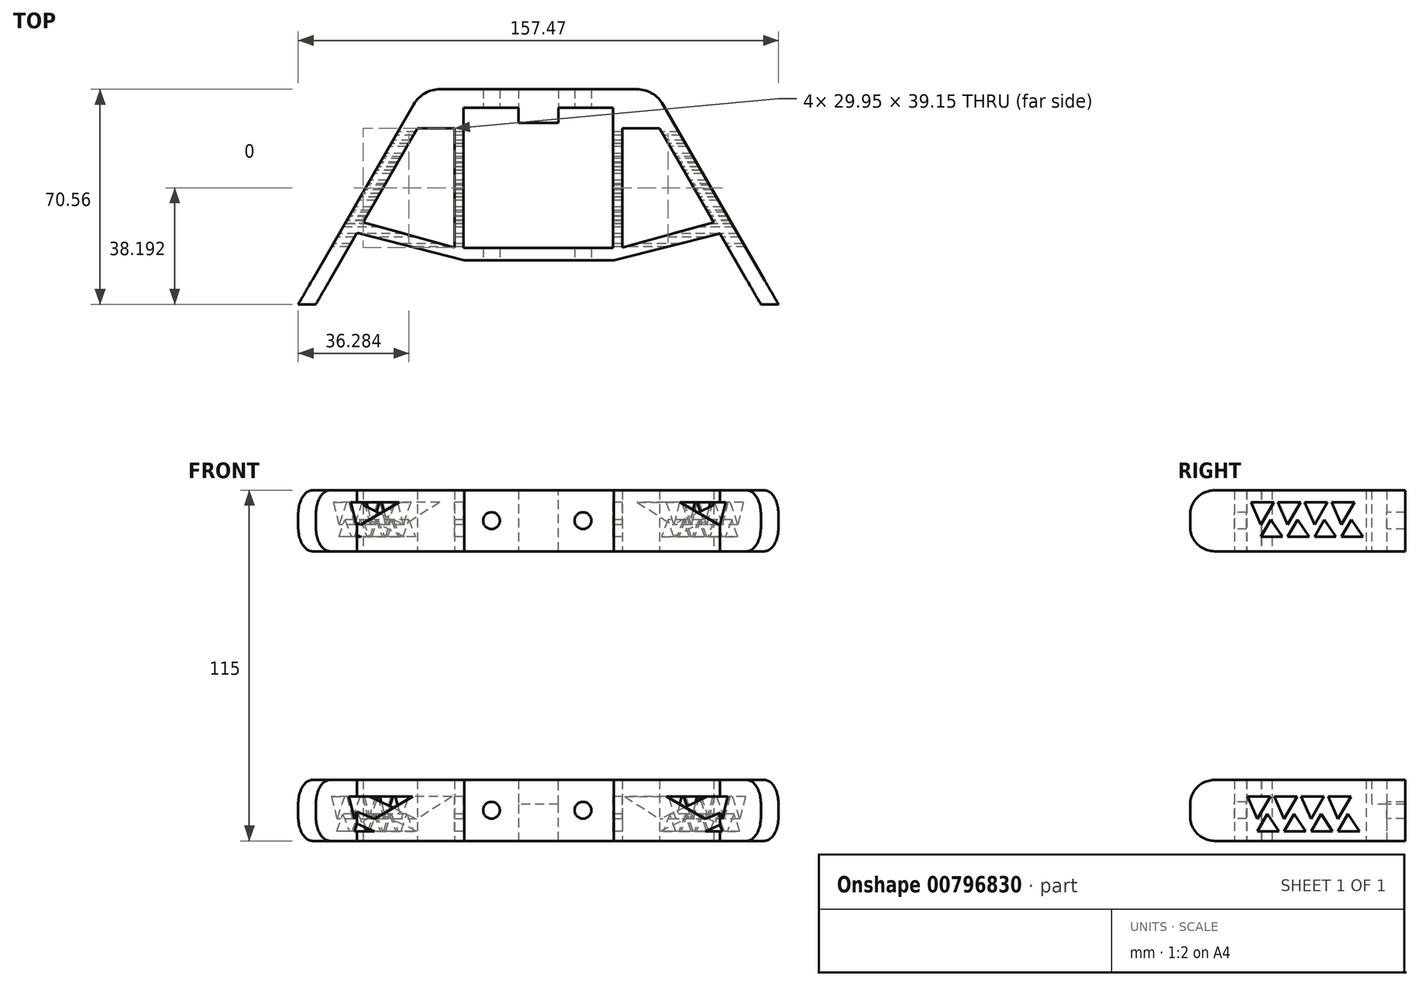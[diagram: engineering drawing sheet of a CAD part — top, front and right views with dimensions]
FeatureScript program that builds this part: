
annotation { "Feature Type Name" : "Feature", "Feature Type Description" : "" }
export const myFeature = defineFeature(function(context is Context, id is Id, definition is map)
    precondition{}
    {
        {
            var Q0;
            Q0=qCreatedBy(makeId("Top.planeOp"),FACE);
            var sketch = newSketch(context, id + "F0", { "sketchPlane" : qUnion([Q0])});
            skLineSegment(sketch, "E0.bottom", {"start": v(24.5, -20.5) * mm, "end": v(-24.5, -20.5) * mm});
            skLineSegment(sketch, "E0.top", {"start": v(24.5, 20.5) * mm, "end": v(-24.5, 20.5) * mm});
            skLineSegment(sketch, "E0.left", {"start": v(24.5, -20.5) * mm, "end": v(24.5, 20.5) * mm});
            skLineSegment(sketch, "E0.right", {"start": v(-24.5, -20.5) * mm, "end": v(-24.5, 20.5) * mm});
            skPoint(sketch, "E0.middle", {"position": v(0, 0) * mm});
            skLineSegment(sketch, "E1", {"start": v(-59.43, -15.52) * mm, "end": v(-72.99, -39) * mm});
            skLineSegment(sketch, "E2", {"start": v(-37.76, 22.02) * mm, "end": v(-37.76, 30.02) * mm, "construction": true});
            skLineSegment(sketch, "E3", {"start": v(35.38, 28.67) * mm, "end": v(35.38, 23.6) * mm, "construction": true});
            skLineSegment(sketch, "E4", {"start": v(-0.03, 31.56) * mm, "end": v(37.97, 31.56) * mm});
            skLineSegment(sketch, "E5", {"start": v(-0.03, 31.56) * mm, "end": v(-38.03, 31.56) * mm});
            skLineSegment(sketch, "E6", {"start": v(-38.03, 31.56) * mm, "end": v(-78.76, -39) * mm});
            skLineSegment(sketch, "E7", {"start": v(37.97, 31.56) * mm, "end": v(78.71, -39) * mm});
            skLineSegment(sketch, "E8.0", {"start": v(-24.27, -24.5) * mm, "end": v(-59.57, -15.48) * mm});
            skLineSegment(sketch, "E8.1", {"start": v(24.73, -24.5) * mm, "end": v(-24.27, -24.5) * mm});
            skLineSegment(sketch, "E8.2", {"start": v(24.73, -24.5) * mm, "end": v(59.5, -15.74) * mm});
            skLineSegment(sketch, "E9.0", {"start": v(-27.5, -20.5) * mm, "end": v(-27.5, -19.69) * mm});
            skLineSegment(sketch, "E10.1", {"start": v(-27.5, 18.77) * mm, "end": v(-39.64, 18.77) * mm});
            skLineSegment(sketch, "E11", {"start": v(-39.64, 18.77) * mm, "end": v(-57.45, -12.1) * mm});
            skLineSegment(sketch, "E12", {"start": v(-57.45, -12.1) * mm, "end": v(-27.5, -20.38) * mm});
            skLineSegment(sketch, "E13.trimOffspring", {"start": v(-27.5, -20.38) * mm, "end": v(-27.5, 18.77) * mm});
            skLineSegment(sketch, "E14.MirrorCS", {"start": v(27.5, -20.38) * mm, "end": v(27.5, 18.77) * mm});
            skLineSegment(sketch, "E15.MirrorCS", {"start": v(39.64, 18.77) * mm, "end": v(57.45, -12.1) * mm});
            skLineSegment(sketch, "E16.MirrorCS", {"start": v(27.5, 18.77) * mm, "end": v(39.64, 18.77) * mm});
            skLineSegment(sketch, "E17.MirrorCS", {"start": v(57.45, -12.1) * mm, "end": v(27.5, -20.38) * mm});
            skLineSegment(sketch, "E18", {"start": v(-78.76, -39) * mm, "end": v(-72.99, -39) * mm});
            skLineSegment(sketch, "E19", {"start": v(78.71, -39) * mm, "end": v(72.94, -39) * mm});
            skPoint(sketch, "E20.orphan", {"position": v(72.9, -44.1) * mm});
            skPoint(sketch, "E21.orphan", {"position": v(-75.93, -44.1) * mm});
            skLineSegment(sketch, "E22", {"start": v(59.5, -15.74) * mm, "end": v(72.94, -39) * mm});
            skSolve(sketch);
        }
        {
            var Q0;
            Q0=makeQuery(id+"F0.imprint","IMPRINT",FACE,{"disambiguationData":[TD([[makeQuery(id+"F0.imprint","IMPRINT",EDGE,{"derivedFrom":sQuery(id+"F0.wireOp",EDGE,"E0.top")}),-1.0]])]});
            var Q1;
            {var subQ1=sQuery(id+"F0.wireOp",EDGE,"E0.bottom");Q1=makeQuery(id+"F0.imprint","IMPRINT",FACE,{"disambiguationData":[TD([[makeQuery(id+"F0.imprint","IMPRINT",EDGE,{"derivedFrom":subQ1}),1.0]])]});}
            extrude(context, id + "F1", {"entities" : qUnion([Q0, Q1]), "depth" : 20 * mm, "offsetDistance" : 25 * mm});
        }
        {
            var Q0;
            Q0=makeQuery(id+"F1.opExtrude","SWEPT_EDGE",EDGE,{"disambiguationData":[OSD([sQuery(id+"F0.wireOp",EDGE,"E4"),sQuery(id+"F0.wireOp",EDGE,"E7")])]});
            var Q1;
            Q1=makeQuery(id+"F1.opExtrude","SWEPT_EDGE",EDGE,{"disambiguationData":[OSD([sQuery(id+"F0.wireOp",EDGE,"E5"),sQuery(id+"F0.wireOp",EDGE,"E6")])]});
            fillet(context, id + "F2", {"entities" : qUnion([Q0, Q1]), "radius" : 10 * mm, "tangentPropagation" : true, "allowEdgeOverflow" : false});
        }
        {
            var Q0;
            Q0=makeQuery(id+"F1.opExtrude","SWEPT_FACE",FACE,{"disambiguationData":[OSD([sQuery(id+"F0.wireOp",EDGE,"E0.top")])]});
            var sketch = newSketch(context, id + "F3", { "sketchPlane" : qUnion([Q0])});
            skLineSegment(sketch, "E23", {"start": v(-24.5, 10) * mm, "end": v(24.5, 10) * mm, "construction": true});
            skLineSegment(sketch, "E24", {"start": v(0, 0) * mm, "end": v(0, 20) * mm, "construction": true});
            skLineSegment(sketch, "E25", {"start": v(0, 10) * mm, "end": v(15, 10) * mm, "construction": true});
            skLineSegment(sketch, "E26", {"start": v(0, 10) * mm, "end": v(-15, 10) * mm, "construction": true});
            skPoint(sketch, "E27", {"position": v(-15, 10) * mm});
            skPoint(sketch, "E28", {"position": v(15, 10) * mm});
            skLineSegment(sketch, "E29", {"start": v(-24.5, 10) * mm, "end": v(-6.5, 10) * mm, "construction": true});
            skLineSegment(sketch, "E30", {"start": v(-6.5, 10) * mm, "end": v(24.5, 10) * mm, "construction": true});
            skLineSegment(sketch, "E31", {"start": v(-6.5, 10) * mm, "end": v(-6.5, 0) * mm});
            skLineSegment(sketch, "E32", {"start": v(-6.5, 10) * mm, "end": v(-6.5, 20) * mm});
            skLineSegment(sketch, "E33.MirrorCS", {"start": v(6.5, 10) * mm, "end": v(6.5, 20) * mm});
            skLineSegment(sketch, "E34.MirrorCS", {"start": v(6.5, 10) * mm, "end": v(6.5, 0) * mm});
            skSolve(sketch);
        }
        {
            var Q0;
            Q0=makeQuery(id+"F1.opExtrude","SWEPT_FACE",FACE,{"disambiguationData":[OSD([sQuery(id+"F0.wireOp",EDGE,"E8.1")])]});
            var sketch = newSketch(context, id + "F4", { "sketchPlane" : qUnion([Q0])});
            skLineSegment(sketch, "E35", {"start": v(-24.9, 10.05) * mm, "end": v(24.1, 10.05) * mm, "construction": true});
            skLineSegment(sketch, "E36", {"start": v(-0.4, 0.05) * mm, "end": v(-0.4, 20.05) * mm, "construction": true});
            skLineSegment(sketch, "E37", {"start": v(-0.4, 10.05) * mm, "end": v(14.6, 10.05) * mm, "construction": true});
            skLineSegment(sketch, "E38", {"start": v(-0.4, 10.05) * mm, "end": v(-15.4, 10.05) * mm, "construction": true});
            skPoint(sketch, "E39", {"position": v(-15.4, 10.05) * mm});
            skPoint(sketch, "E40", {"position": v(14.6, 10.05) * mm});
            skSolve(sketch);
        }
        {
            var Q0;
            Q0=sQuery(id+"F4.wireOp",VERTEX,"E39");
            var Q1;
            Q1=sQuery(id+"F4.wireOp",VERTEX,"E40");
            var Q2;
            Q2=makeQuery(id+"F1.opExtrude","SWEPT_BODY",BODY,{"disambiguationData":[OSD([sQuery(id+"F0.wireOp",EDGE,"E0.bottom"),sQuery(id+"F0.wireOp",EDGE,"E0.top"),sQuery(id+"F0.wireOp",EDGE,"E0.left"),sQuery(id+"F0.wireOp",EDGE,"E0.right"),sQuery(id+"F0.wireOp",EDGE,"E1"),sQuery(id+"F0.wireOp",EDGE,"E4"),sQuery(id+"F0.wireOp",EDGE,"E5"),sQuery(id+"F0.wireOp",EDGE,"E6"),sQuery(id+"F0.wireOp",EDGE,"E7"),sQuery(id+"F0.wireOp",EDGE,"E8.0"),sQuery(id+"F0.wireOp",EDGE,"E8.1"),sQuery(id+"F0.wireOp",EDGE,"E8.2"),sQuery(id+"F0.wireOp",EDGE,"E10.1"),sQuery(id+"F0.wireOp",EDGE,"E11"),sQuery(id+"F0.wireOp",EDGE,"E12"),sQuery(id+"F0.wireOp",EDGE,"E13.trimOffspring"),sQuery(id+"F0.wireOp",EDGE,"E14.MirrorCS"),sQuery(id+"F0.wireOp",EDGE,"E15.MirrorCS"),sQuery(id+"F0.wireOp",EDGE,"E16.MirrorCS"),sQuery(id+"F0.wireOp",EDGE,"E17.MirrorCS"),sQuery(id+"F0.wireOp",EDGE,"E18"),sQuery(id+"F0.wireOp",EDGE,"E19"),sQuery(id+"F0.wireOp",EDGE,"E22")])]});
            hole(context, id + "F5", {"style" : HoleStyle.SIMPLE, "endStyle" : HoleEndStyle.THROUGH, "holeDiameter" : 5.5 * mm, "majorDiameter" : 5 * mm, "isTappedThrough" : true, "tappedDepth" : 12 * mm, "tapClearance" : 3, "locations" : qUnion([Q0, Q1]), "scope" : qUnion([Q2])});
        }
        {
            var Q0;
            {var subQ3=sQuery(id+"F3.wireOp",EDGE,"E31");Q0=makeQuery(id+"F3.imprint","IMPRINT",FACE,{"disambiguationData":[TD([[makeQuery(id+"F3.imprint","IMPRINT",EDGE,{"derivedFrom":subQ3}),-1.0]])]});}
            var Q1;
            {var subQ4=sQuery(id+"F3.wireOp",EDGE,"E33.MirrorCS");Q1=makeQuery(id+"F3.imprint","IMPRINT",FACE,{"disambiguationData":[TD([[makeQuery(id+"F3.imprint","IMPRINT",EDGE,{"derivedFrom":subQ4}),-1.0]])]});}
            extrude(context, id + "F6", {"entities" : qUnion([Q0, Q1]), "operationType" : NewBodyOperationType.REMOVE, "oppositeDirection" : true, "depth" : 5 * mm, "offsetDistance" : 25 * mm});
        }
        {
            var Q0;
            Q0=makeQuery(id+"F1.opExtrude","SWEPT_BODY",BODY,{"disambiguationData":[OSD([sQuery(id+"F0.wireOp",EDGE,"E0.bottom"),sQuery(id+"F0.wireOp",EDGE,"E0.top"),sQuery(id+"F0.wireOp",EDGE,"E0.left"),sQuery(id+"F0.wireOp",EDGE,"E0.right"),sQuery(id+"F0.wireOp",EDGE,"E1"),sQuery(id+"F0.wireOp",EDGE,"E4"),sQuery(id+"F0.wireOp",EDGE,"E5"),sQuery(id+"F0.wireOp",EDGE,"E6"),sQuery(id+"F0.wireOp",EDGE,"E7"),sQuery(id+"F0.wireOp",EDGE,"E8.0"),sQuery(id+"F0.wireOp",EDGE,"E8.1"),sQuery(id+"F0.wireOp",EDGE,"E8.2"),sQuery(id+"F0.wireOp",EDGE,"E10.1"),sQuery(id+"F0.wireOp",EDGE,"E11"),sQuery(id+"F0.wireOp",EDGE,"E12"),sQuery(id+"F0.wireOp",EDGE,"E13.trimOffspring"),sQuery(id+"F0.wireOp",EDGE,"E14.MirrorCS"),sQuery(id+"F0.wireOp",EDGE,"E15.MirrorCS"),sQuery(id+"F0.wireOp",EDGE,"E16.MirrorCS"),sQuery(id+"F0.wireOp",EDGE,"E17.MirrorCS"),sQuery(id+"F0.wireOp",EDGE,"E18"),sQuery(id+"F0.wireOp",EDGE,"E19"),sQuery(id+"F0.wireOp",EDGE,"E22")])]});
            transform(context, id + "F7", {"entities" : qUnion([Q0]), "transformType" : TransformType.COPY});
        }
        {
            var Q0;
            Q0=makeQuery(id+"F7.opPattern","COPY",BODY,{"derivedFrom":makeQuery(id+"F1.opExtrude","SWEPT_BODY",BODY,{"disambiguationData":[OSD([sQuery(id+"F0.wireOp",EDGE,"E0.bottom"),sQuery(id+"F0.wireOp",EDGE,"E0.top"),sQuery(id+"F0.wireOp",EDGE,"E0.left"),sQuery(id+"F0.wireOp",EDGE,"E0.right"),sQuery(id+"F0.wireOp",EDGE,"E1"),sQuery(id+"F0.wireOp",EDGE,"E4"),sQuery(id+"F0.wireOp",EDGE,"E5"),sQuery(id+"F0.wireOp",EDGE,"E6"),sQuery(id+"F0.wireOp",EDGE,"E7"),sQuery(id+"F0.wireOp",EDGE,"E8.0"),sQuery(id+"F0.wireOp",EDGE,"E8.1"),sQuery(id+"F0.wireOp",EDGE,"E8.2"),sQuery(id+"F0.wireOp",EDGE,"E10.1"),sQuery(id+"F0.wireOp",EDGE,"E11"),sQuery(id+"F0.wireOp",EDGE,"E12"),sQuery(id+"F0.wireOp",EDGE,"E13.trimOffspring"),sQuery(id+"F0.wireOp",EDGE,"E14.MirrorCS"),sQuery(id+"F0.wireOp",EDGE,"E15.MirrorCS"),sQuery(id+"F0.wireOp",EDGE,"E16.MirrorCS"),sQuery(id+"F0.wireOp",EDGE,"E17.MirrorCS"),sQuery(id+"F0.wireOp",EDGE,"E18"),sQuery(id+"F0.wireOp",EDGE,"E19"),sQuery(id+"F0.wireOp",EDGE,"E22")])]}),"instanceName":"1"});
            transform(context, id + "F8", {"entities" : qUnion([Q0]), "transformType" : TransformType.TRANSLATION_3D, "dx" : 0 * mm, "dy" : 0 * mm, "dz" : -95 * mm, "makeCopy" : false});
        }
        {
            var Q0;
            Q0=makeQuery(id+"F7.opPattern","COPY",FACE,{"derivedFrom":makeQuery(id+"F1.opExtrude","SWEPT_FACE",FACE,{"disambiguationData":[OSD([sQuery(id+"F0.wireOp",EDGE,"E0.top")])]}),"instanceName":"1"});
            var sketch = newSketch(context, id + "F9", { "sketchPlane" : qUnion([Q0])});
            skLineSegment(sketch, "E41", {"start": v(0, -95) * mm, "end": v(0, -83) * mm, "construction": true});
            skLineSegment(sketch, "E42", {"start": v(6.5, -83) * mm, "end": v(-6.5, -83) * mm});
            skSolve(sketch);
        }
        {
            var Q0;
            {var subQ0=sQuery(id+"F9.wireOp",EDGE,"E42");Q0=makeQuery(id+"F9.imprint","IMPRINT",FACE,{"disambiguationData":[TD([[makeQuery(id+"F9.imprint","IMPRINT",EDGE,{"derivedFrom":subQ0}),1.0]])]});}
            var Q1;
            Q1=makeQuery(id+"F7.opPattern","COPY",FACE,{"derivedFrom":makeQuery(id+"F1.opExtrude","SWEPT_FACE",FACE,{"disambiguationData":[OSD([sQuery(id+"F0.wireOp",EDGE,"E4"),sQuery(id+"F0.wireOp",EDGE,"E5")])]}),"instanceName":"1"});
            extrude(context, id + "F10", {"entities" : qUnion([Q0]), "operationType" : NewBodyOperationType.REMOVE, "endBound" : BoundingType.UP_TO_SURFACE, "oppositeDirection" : true, "depth" : 25 * mm, "endBoundEntityFace" : qUnion([Q1]), "offsetDistance" : 25 * mm});
        }
        {
            var Q0;
            {var subQ0=sQuery(id+"F0.wireOp",EDGE,"E0.right");Q0=makeQuery(id+"F6.boolean.opBoolean","MERGE",FACE,{"derivedFrom":[makeQuery(id+"F1.opExtrude","SWEPT_FACE",FACE,{"disambiguationData":[OSD([subQ0])]}),makeQuery(id+"F6.opExtrude","SWEPT_FACE",FACE,{"disambiguationData":[OSD([sQuery(id+"F0.wireOp",EDGE,"E0.top"),subQ0])]})]});}
            var sketch = newSketch(context, id + "F11", { "sketchPlane" : qUnion([Q0])});
            skLineSegment(sketch, "E43", {"start": v(-15.83, 4.73) * mm, "end": v(-8.76, 4.73) * mm});
            skLineSegment(sketch, "E44", {"start": v(-8.76, 4.73) * mm, "end": v(-12.54, 10.42) * mm});
            skLineSegment(sketch, "E45", {"start": v(-12.54, 10.42) * mm, "end": v(-15.83, 4.73) * mm});
            skLineSegment(sketch, "E46", {"start": v(-15.83, 8.68) * mm, "end": v(-11.54, 16.1) * mm});
            skLineSegment(sketch, "E47", {"start": v(-11.54, 16.1) * mm, "end": v(-19.04, 16.1) * mm});
            skLineSegment(sketch, "E48", {"start": v(-15.83, 8.68) * mm, "end": v(-19.04, 16.1) * mm});
            skLineSegment(sketch, "E49.1.0.0", {"start": v(-7.03, 8.68) * mm, "end": v(-10.24, 16.1) * mm});
            skLineSegment(sketch, "E49.1.0.1", {"start": v(-2.74, 16.1) * mm, "end": v(-10.24, 16.1) * mm});
            skLineSegment(sketch, "E49.1.0.2", {"start": v(-7.03, 8.68) * mm, "end": v(-2.74, 16.1) * mm});
            skLineSegment(sketch, "E49.1.0.3", {"start": v(-3.74, 10.42) * mm, "end": v(-7.03, 4.73) * mm});
            skLineSegment(sketch, "E49.1.0.4", {"start": v(0.04, 4.73) * mm, "end": v(-3.74, 10.42) * mm});
            skLineSegment(sketch, "E49.1.0.5", {"start": v(-7.03, 4.73) * mm, "end": v(0.04, 4.73) * mm});
            skLineSegment(sketch, "E49.2.0.0", {"start": v(1.77, 8.68) * mm, "end": v(-1.44, 16.1) * mm});
            skLineSegment(sketch, "E49.2.0.1", {"start": v(6.06, 16.1) * mm, "end": v(-1.44, 16.1) * mm});
            skLineSegment(sketch, "E49.2.0.2", {"start": v(1.77, 8.68) * mm, "end": v(6.06, 16.1) * mm});
            skLineSegment(sketch, "E49.2.0.3", {"start": v(5.06, 10.42) * mm, "end": v(1.77, 4.73) * mm});
            skLineSegment(sketch, "E49.2.0.4", {"start": v(8.84, 4.73) * mm, "end": v(5.06, 10.42) * mm});
            skLineSegment(sketch, "E49.2.0.5", {"start": v(1.77, 4.73) * mm, "end": v(8.84, 4.73) * mm});
            skLineSegment(sketch, "E49.3.0.0", {"start": v(10.57, 8.68) * mm, "end": v(7.36, 16.1) * mm});
            skLineSegment(sketch, "E49.3.0.1", {"start": v(14.86, 16.1) * mm, "end": v(7.36, 16.1) * mm});
            skLineSegment(sketch, "E49.3.0.2", {"start": v(10.57, 8.68) * mm, "end": v(14.86, 16.1) * mm});
            skLineSegment(sketch, "E49.3.0.3", {"start": v(13.86, 10.42) * mm, "end": v(10.57, 4.73) * mm});
            skLineSegment(sketch, "E49.3.0.4", {"start": v(17.64, 4.73) * mm, "end": v(13.86, 10.42) * mm});
            skLineSegment(sketch, "E49.3.0.5", {"start": v(10.57, 4.73) * mm, "end": v(17.64, 4.73) * mm});
            skLineSegment(sketch, "E49.direction1", {"start": v(-15.83, 8.68) * mm, "end": v(-7.03, 8.68) * mm, "construction": true});
            skSolve(sketch);
        }
        {
            var Q0;
            Q0=makeQuery(id+"F11.imprint","IMPRINT",FACE,{"disambiguationData":[TD([[makeQuery(id+"F11.imprint","IMPRINT",EDGE,{"derivedFrom":sQuery(id+"F11.wireOp",EDGE,"E46")}),1.0]])]});
            var Q1;
            Q1=makeQuery(id+"F11.imprint","IMPRINT",FACE,{"disambiguationData":[TD([[makeQuery(id+"F11.imprint","IMPRINT",EDGE,{"derivedFrom":sQuery(id+"F11.wireOp",EDGE,"E43")}),1.0]])]});
            var Q2;
            Q2=makeQuery(id+"F11.imprint","IMPRINT",FACE,{"disambiguationData":[TD([[makeQuery(id+"F11.imprint","IMPRINT",EDGE,{"derivedFrom":sQuery(id+"F11.wireOp",EDGE,"E49.1.0.0")}),-1.0]])]});
            var Q3;
            Q3=makeQuery(id+"F11.imprint","IMPRINT",FACE,{"disambiguationData":[TD([[makeQuery(id+"F11.imprint","IMPRINT",EDGE,{"derivedFrom":sQuery(id+"F11.wireOp",EDGE,"E49.1.0.3")}),1.0]])]});
            var Q4;
            Q4=makeQuery(id+"F11.imprint","IMPRINT",FACE,{"disambiguationData":[TD([[makeQuery(id+"F11.imprint","IMPRINT",EDGE,{"derivedFrom":sQuery(id+"F11.wireOp",EDGE,"E49.2.0.0")}),-1.0]])]});
            var Q5;
            Q5=makeQuery(id+"F11.imprint","IMPRINT",FACE,{"disambiguationData":[TD([[makeQuery(id+"F11.imprint","IMPRINT",EDGE,{"derivedFrom":sQuery(id+"F11.wireOp",EDGE,"E49.2.0.3")}),1.0]])]});
            var Q6;
            Q6=makeQuery(id+"F11.imprint","IMPRINT",FACE,{"disambiguationData":[TD([[makeQuery(id+"F11.imprint","IMPRINT",EDGE,{"derivedFrom":sQuery(id+"F11.wireOp",EDGE,"E49.3.0.0")}),-1.0]])]});
            var Q7;
            Q7=makeQuery(id+"F11.imprint","IMPRINT",FACE,{"disambiguationData":[TD([[makeQuery(id+"F11.imprint","IMPRINT",EDGE,{"derivedFrom":sQuery(id+"F11.wireOp",EDGE,"E49.3.0.3")}),1.0]])]});
            extrude(context, id + "F12", {"entities" : qUnion([Q0, Q1, Q2, Q3, Q4, Q5, Q6, Q7]), "operationType" : NewBodyOperationType.REMOVE, "endBound" : BoundingType.SYMMETRIC, "depth" : 200 * mm, "offsetDistance" : 25 * mm});
        }
        {
            var Q0;
            {var subQ0=sQuery(id+"F0.wireOp",EDGE,"E0.right");Q0=makeQuery(id+"F7.opPattern","COPY",FACE,{"derivedFrom":makeQuery(id+"F6.boolean.opBoolean","MERGE",FACE,{"derivedFrom":[makeQuery(id+"F1.opExtrude","SWEPT_FACE",FACE,{"disambiguationData":[OSD([subQ0])]}),makeQuery(id+"F6.opExtrude","SWEPT_FACE",FACE,{"disambiguationData":[OSD([sQuery(id+"F0.wireOp",EDGE,"E0.top"),subQ0])]})]}),"instanceName":"1"});}
            var sketch = newSketch(context, id + "F13", { "sketchPlane" : qUnion([Q0])});
            skLineSegment(sketch, "E50", {"start": v(-16.96, -91.82) * mm, "end": v(-9.88, -91.82) * mm});
            skLineSegment(sketch, "E51", {"start": v(-9.88, -91.82) * mm, "end": v(-13.67, -86.13) * mm});
            skLineSegment(sketch, "E52", {"start": v(-13.67, -86.13) * mm, "end": v(-16.96, -91.82) * mm});
            skLineSegment(sketch, "E53", {"start": v(-16.96, -87.87) * mm, "end": v(-12.67, -80.45) * mm});
            skLineSegment(sketch, "E54", {"start": v(-12.67, -80.45) * mm, "end": v(-20.16, -80.45) * mm});
            skLineSegment(sketch, "E55", {"start": v(-16.96, -87.87) * mm, "end": v(-20.16, -80.45) * mm});
            skLineSegment(sketch, "E56.1.0.0", {"start": v(-8.16, -87.87) * mm, "end": v(-11.36, -80.45) * mm});
            skLineSegment(sketch, "E56.1.0.1", {"start": v(-3.87, -80.45) * mm, "end": v(-11.36, -80.45) * mm});
            skLineSegment(sketch, "E56.1.0.2", {"start": v(-8.16, -87.87) * mm, "end": v(-3.87, -80.45) * mm});
            skLineSegment(sketch, "E56.1.0.3", {"start": v(-4.87, -86.13) * mm, "end": v(-8.16, -91.82) * mm});
            skLineSegment(sketch, "E56.1.0.4", {"start": v(-1.08, -91.82) * mm, "end": v(-4.87, -86.13) * mm});
            skLineSegment(sketch, "E56.1.0.5", {"start": v(-8.16, -91.82) * mm, "end": v(-1.08, -91.82) * mm});
            skLineSegment(sketch, "E56.2.0.0", {"start": v(0.64, -87.87) * mm, "end": v(-2.56, -80.45) * mm});
            skLineSegment(sketch, "E56.2.0.1", {"start": v(4.93, -80.45) * mm, "end": v(-2.56, -80.45) * mm});
            skLineSegment(sketch, "E56.2.0.2", {"start": v(0.64, -87.87) * mm, "end": v(4.93, -80.45) * mm});
            skLineSegment(sketch, "E56.2.0.3", {"start": v(3.93, -86.13) * mm, "end": v(0.64, -91.82) * mm});
            skLineSegment(sketch, "E56.2.0.4", {"start": v(7.72, -91.82) * mm, "end": v(3.93, -86.13) * mm});
            skLineSegment(sketch, "E56.2.0.5", {"start": v(0.64, -91.82) * mm, "end": v(7.72, -91.82) * mm});
            skLineSegment(sketch, "E56.3.0.0", {"start": v(9.44, -87.87) * mm, "end": v(6.24, -80.45) * mm});
            skLineSegment(sketch, "E56.3.0.1", {"start": v(13.73, -80.45) * mm, "end": v(6.24, -80.45) * mm});
            skLineSegment(sketch, "E56.3.0.2", {"start": v(9.44, -87.87) * mm, "end": v(13.73, -80.45) * mm});
            skLineSegment(sketch, "E56.3.0.3", {"start": v(12.73, -86.13) * mm, "end": v(9.44, -91.82) * mm});
            skLineSegment(sketch, "E56.3.0.4", {"start": v(16.52, -91.82) * mm, "end": v(12.73, -86.13) * mm});
            skLineSegment(sketch, "E56.3.0.5", {"start": v(9.44, -91.82) * mm, "end": v(16.52, -91.82) * mm});
            skLineSegment(sketch, "E56.direction1", {"start": v(-16.96, -87.87) * mm, "end": v(-8.16, -87.87) * mm, "construction": true});
            skSolve(sketch);
        }
        {
            var Q0;
            Q0=makeQuery(id+"F13.imprint","IMPRINT",FACE,{"disambiguationData":[TD([[makeQuery(id+"F13.imprint","IMPRINT",EDGE,{"derivedFrom":sQuery(id+"F13.wireOp",EDGE,"E53")}),1.0]])]});
            var Q1;
            Q1=makeQuery(id+"F13.imprint","IMPRINT",FACE,{"disambiguationData":[TD([[makeQuery(id+"F13.imprint","IMPRINT",EDGE,{"derivedFrom":sQuery(id+"F13.wireOp",EDGE,"E50")}),1.0]])]});
            var Q2;
            Q2=makeQuery(id+"F13.imprint","IMPRINT",FACE,{"disambiguationData":[TD([[makeQuery(id+"F13.imprint","IMPRINT",EDGE,{"derivedFrom":sQuery(id+"F13.wireOp",EDGE,"E56.1.0.3")}),1.0]])]});
            var Q3;
            Q3=makeQuery(id+"F13.imprint","IMPRINT",FACE,{"disambiguationData":[TD([[makeQuery(id+"F13.imprint","IMPRINT",EDGE,{"derivedFrom":sQuery(id+"F13.wireOp",EDGE,"E56.1.0.0")}),-1.0]])]});
            var Q4;
            Q4=makeQuery(id+"F13.imprint","IMPRINT",FACE,{"disambiguationData":[TD([[makeQuery(id+"F13.imprint","IMPRINT",EDGE,{"derivedFrom":sQuery(id+"F13.wireOp",EDGE,"E56.2.0.0")}),-1.0]])]});
            var Q5;
            Q5=makeQuery(id+"F13.imprint","IMPRINT",FACE,{"disambiguationData":[TD([[makeQuery(id+"F13.imprint","IMPRINT",EDGE,{"derivedFrom":sQuery(id+"F13.wireOp",EDGE,"E56.2.0.3")}),1.0]])]});
            var Q6;
            Q6=makeQuery(id+"F13.imprint","IMPRINT",FACE,{"disambiguationData":[TD([[makeQuery(id+"F13.imprint","IMPRINT",EDGE,{"derivedFrom":sQuery(id+"F13.wireOp",EDGE,"E56.3.0.0")}),-1.0]])]});
            var Q7;
            Q7=makeQuery(id+"F13.imprint","IMPRINT",FACE,{"disambiguationData":[TD([[makeQuery(id+"F13.imprint","IMPRINT",EDGE,{"derivedFrom":sQuery(id+"F13.wireOp",EDGE,"E56.3.0.3")}),1.0]])]});
            extrude(context, id + "F14", {"entities" : qUnion([Q0, Q1, Q2, Q3, Q4, Q5, Q6, Q7]), "operationType" : NewBodyOperationType.REMOVE, "endBound" : BoundingType.SYMMETRIC, "depth" : 200 * mm, "offsetDistance" : 25 * mm});
        }
        {
            var Q0;
            Q0=makeQuery(id+"F1.opExtrude","CAP_EDGE",EDGE,{"disambiguationData":[OSD([sQuery(id+"F0.wireOp",EDGE,"E18")])],"isStart":false});
            var Q1;
            Q1=makeQuery(id+"F1.opExtrude","CAP_EDGE",EDGE,{"disambiguationData":[OSD([sQuery(id+"F0.wireOp",EDGE,"E18")])],"isStart":true});
            var Q2;
            Q2=makeQuery(id+"F1.opExtrude","CAP_EDGE",EDGE,{"disambiguationData":[OSD([sQuery(id+"F0.wireOp",EDGE,"E19")])],"isStart":false});
            var Q3;
            Q3=makeQuery(id+"F1.opExtrude","CAP_EDGE",EDGE,{"disambiguationData":[OSD([sQuery(id+"F0.wireOp",EDGE,"E19")])],"isStart":true});
            var Q4;
            Q4=makeQuery(id+"F7.opPattern","COPY",EDGE,{"derivedFrom":makeQuery(id+"F1.opExtrude","CAP_EDGE",EDGE,{"disambiguationData":[OSD([sQuery(id+"F0.wireOp",EDGE,"E18")])],"isStart":false}),"instanceName":"1"});
            var Q5;
            Q5=makeQuery(id+"F7.opPattern","COPY",EDGE,{"derivedFrom":makeQuery(id+"F1.opExtrude","CAP_EDGE",EDGE,{"disambiguationData":[OSD([sQuery(id+"F0.wireOp",EDGE,"E18")])],"isStart":true}),"instanceName":"1"});
            var Q6;
            Q6=makeQuery(id+"F7.opPattern","COPY",EDGE,{"derivedFrom":makeQuery(id+"F1.opExtrude","CAP_EDGE",EDGE,{"disambiguationData":[OSD([sQuery(id+"F0.wireOp",EDGE,"E19")])],"isStart":false}),"instanceName":"1"});
            var Q7;
            Q7=makeQuery(id+"F7.opPattern","COPY",EDGE,{"derivedFrom":makeQuery(id+"F1.opExtrude","CAP_EDGE",EDGE,{"disambiguationData":[OSD([sQuery(id+"F0.wireOp",EDGE,"E19")])],"isStart":true}),"instanceName":"1"});
            fillet(context, id + "F15", {"entities" : qUnion([Q0, Q1, Q2, Q3, Q4, Q5, Q6, Q7]), "radius" : 8 * mm, "tangentPropagation" : true, "allowEdgeOverflow" : false});
        }
    });
